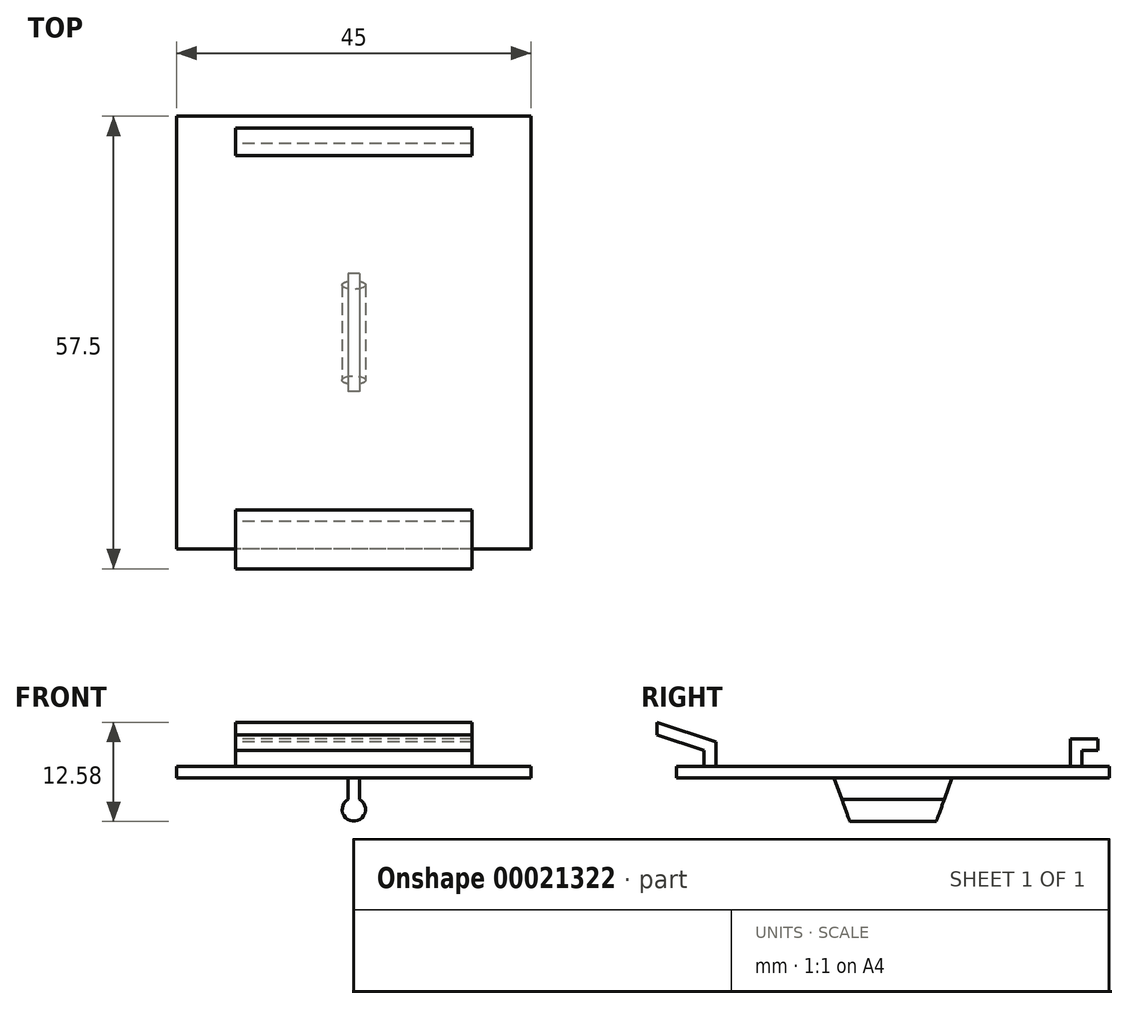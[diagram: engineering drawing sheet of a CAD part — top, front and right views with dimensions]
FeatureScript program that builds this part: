
annotation { "Feature Type Name" : "Feature", "Feature Type Description" : "" }
export const myFeature = defineFeature(function(context is Context, id is Id, definition is map)
    precondition{}
    {
        {
            var Q0;
            Q0=qCreatedBy(makeId("Top.planeOp"),FACE);
            var sketch = newSketch(context, id + "F0", { "sketchPlane" : qUnion([Q0])});
            skLineSegment(sketch, "E0.rect.bottom", {"start": v(22.5, 27.5) * mm, "end": v(-22.5, 27.5) * mm});
            skLineSegment(sketch, "E0.rect.top", {"start": v(22.5, -27.5) * mm, "end": v(-22.5, -27.5) * mm});
            skLineSegment(sketch, "E0.rect.left", {"start": v(22.5, 27.5) * mm, "end": v(22.5, -27.5) * mm});
            skLineSegment(sketch, "E0.rect.right", {"start": v(-22.5, 27.5) * mm, "end": v(-22.5, -27.5) * mm});
            skPoint(sketch, "E0.rect.middle", {"position": v(0, 0) * mm});
            skSolve(sketch);
        }
        {
            var Q0;
            Q0=makeQuery(id+"F0.imprint","IMPRINT",FACE,{"disambiguationData":[TD([[makeQuery(id+"F0.imprint","IMPRINT",EDGE,{"derivedFrom":sQuery(id+"F0.wireOp",EDGE,"E0.rect.bottom")}),1.0]])]});
            extrude(context, id + "F1", {"entities" : qUnion([Q0]), "oppositeDirection" : true, "depth" : 1.5 * mm});
        }
        {
            var Q0;
            Q0=qCreatedBy(makeId("Right.planeOp"),FACE);
            var sketch = newSketch(context, id + "F2", { "sketchPlane" : qUnion([Q0])});
            skLineSegment(sketch, "E1", {"start": v(-24, 2) * mm, "end": v(-30, 4) * mm});
            skLineSegment(sketch, "E2", {"start": v(-24, 2) * mm, "end": v(-24, 0) * mm});
            skLineSegment(sketch, "E3.0", {"start": v(-22.5, 3.08) * mm, "end": v(-30, 5.58) * mm});
            skLineSegment(sketch, "E3.1", {"start": v(-22.5, 3.08) * mm, "end": v(-22.5, 0) * mm});
            skLineSegment(sketch, "E4", {"start": v(-30, 5.58) * mm, "end": v(-30, 4) * mm});
            skLineSegment(sketch, "E5", {"start": v(-24, 0) * mm, "end": v(-22.5, 0) * mm});
            skLineSegment(sketch, "E6", {"start": v(22.5, 0) * mm, "end": v(22.5, 3.5) * mm});
            skLineSegment(sketch, "E7", {"start": v(26, 3.5) * mm, "end": v(26, 2) * mm});
            skLineSegment(sketch, "E8", {"start": v(26, 2) * mm, "end": v(24, 2) * mm});
            skLineSegment(sketch, "E9", {"start": v(24, 2) * mm, "end": v(24, 0) * mm});
            skLineSegment(sketch, "E10", {"start": v(24, 0) * mm, "end": v(22.5, 0) * mm});
            skLineSegment(sketch, "E11", {"start": v(22.5, 3.5) * mm, "end": v(26, 3.5) * mm});
            skLineSegment(sketch, "E12", {"start": v(-24, 0) * mm, "end": v(-27.5, 0) * mm, "construction": true});
            skLineSegment(sketch, "E13", {"start": v(24, 0) * mm, "end": v(27.5, 0) * mm, "construction": true});
            skSolve(sketch);
        }
        {
            var Q0;
            Q0 = qSketchRegion(id + "F2", true);
            extrude(context, id + "F3", {"entities" : qUnion([Q0]), "operationType" : NewBodyOperationType.ADD, "endBound" : BoundingType.SYMMETRIC, "depth" : 30 * mm});
        }
        {
            var Q0;
            Q0=makeQuery(id+"F1.opExtrude","CAP_FACE",FACE,{"disambiguationData":[OSD([sQuery(id+"F0.wireOp",EDGE,"E0.rect.bottom"),sQuery(id+"F0.wireOp",EDGE,"E0.rect.top"),sQuery(id+"F0.wireOp",EDGE,"E0.rect.left"),sQuery(id+"F0.wireOp",EDGE,"E0.rect.right")])],"isStart":false});
            var sketch = newSketch(context, id + "F4", { "sketchPlane" : qUnion([Q0])});
            skLineSegment(sketch, "E14.rect.bottom", {"start": v(0.75, -7.5) * mm, "end": v(-0.75, -7.5) * mm});
            skLineSegment(sketch, "E14.rect.top", {"start": v(0.75, 7.5) * mm, "end": v(-0.75, 7.5) * mm});
            skLineSegment(sketch, "E14.rect.left", {"start": v(0.75, -7.5) * mm, "end": v(0.75, 7.5) * mm});
            skLineSegment(sketch, "E14.rect.right", {"start": v(-0.75, -7.5) * mm, "end": v(-0.75, 7.5) * mm});
            skPoint(sketch, "E14.rect.middle", {"position": v(0, 0) * mm});
            skSolve(sketch);
        }
        {
            var Q0;
            Q0 = qSketchRegion(id + "F4", true);
            extrude(context, id + "F5", {"entities" : qUnion([Q0]), "operationType" : NewBodyOperationType.ADD, "depth" : 4 * mm});
        }
        {
            var Q0;
            Q0=makeQuery(id+"F5.opExtrude","SWEPT_FACE",FACE,{"disambiguationData":[OSD([sQuery(id+"F4.wireOp",EDGE,"E14.rect.top")])]});
            var sketch = newSketch(context, id + "F6", { "sketchPlane" : qUnion([Q0])});
            skCircle(sketch, "E15", {"center": v(0, -5.5) * mm, "radius": 1.5 * mm});
            skSolve(sketch);
        }
        {
            var Q0;
            Q0 = qSketchRegion(id + "F6", true);
            var Q1;
            Q1=makeQuery(id+"F5.opExtrude","SWEPT_FACE",FACE,{"disambiguationData":[OSD([sQuery(id+"F4.wireOp",EDGE,"E14.rect.bottom")])]});
            extrude(context, id + "F7", {"entities" : qUnion([Q0]), "operationType" : NewBodyOperationType.ADD, "endBound" : BoundingType.UP_TO_SURFACE, "oppositeDirection" : true, "endBoundEntityFace" : qUnion([Q1]), "depth" : 25 * mm});
        }
        {
            var Q0;
            Q0=qCreatedBy(makeId("Right.planeOp"),FACE);
            var sketch = newSketch(context, id + "F8", { "sketchPlane" : qUnion([Q0])});
            skLineSegment(sketch, "E16", {"start": v(-7.5, -1.5) * mm, "end": v(0, -22.1) * mm});
            skLineSegment(sketch, "E17", {"start": v(0, -22.1) * mm, "end": v(7.5, -1.5) * mm});
            skLineSegment(sketch, "E18", {"start": v(0, 0) * mm, "end": v(0, -22.1) * mm, "construction": true});
            skLineSegment(sketch, "E19", {"start": v(-7.5, -1.5) * mm, "end": v(-7.5, -22.1) * mm});
            skLineSegment(sketch, "E20", {"start": v(-7.5, -22.1) * mm, "end": v(7.5, -22.1) * mm});
            skLineSegment(sketch, "E21", {"start": v(7.5, -22.1) * mm, "end": v(7.5, -1.5) * mm});
            skSolve(sketch);
        }
        {
            var Q0;
            Q0 = qSketchRegion(id + "F8", true);
            extrude(context, id + "F9", {"entities" : qUnion([Q0]), "operationType" : NewBodyOperationType.REMOVE, "endBound" : BoundingType.THROUGH_ALL, "oppositeDirection" : true, "depth" : 25 * mm, "hasSecondDirection" : true, "secondDirectionBound" : SecondDirectionBoundingType.THROUGH_ALL, "secondDirectionOppositeDirection" : false, "secondDirectionDepth" : 25 * mm});
        }
    });
